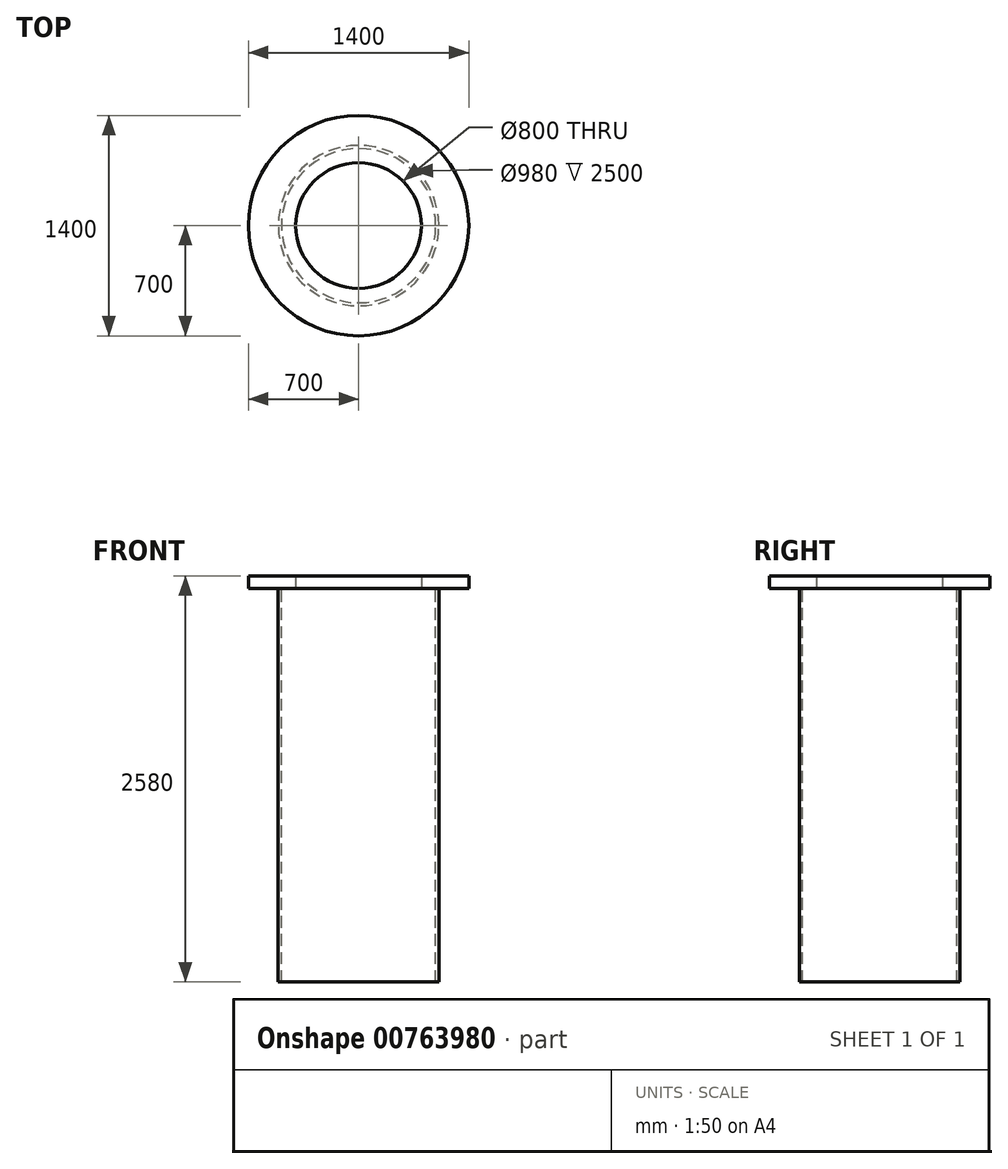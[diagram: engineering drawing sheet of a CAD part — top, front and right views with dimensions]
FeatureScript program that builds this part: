
annotation { "Feature Type Name" : "Feature", "Feature Type Description" : "" }
export const myFeature = defineFeature(function(context is Context, id is Id, definition is map)
    precondition{}
    {
        {
            var Q0;
            Q0=qCreatedBy(makeId("Top.planeOp"),FACE);
            var sketch = newSketch(context, id + "F0", { "sketchPlane" : qUnion([Q0])});
            skCircle(sketch, "E0", {"center": v(0, 0) * mm, "radius": 500 * mm, "construction": true});
            skCircle(sketch, "E1", {"center": v(0, 0) * mm, "radius": 490 * mm});
            skCircle(sketch, "E2", {"center": v(0, 0) * mm, "radius": 510 * mm});
            skCircle(sketch, "E3", {"center": v(0, 0) * mm, "radius": 400 * mm});
            skCircle(sketch, "E4", {"center": v(0, 0) * mm, "radius": 700 * mm});
            skSolve(sketch);
        }
        {
            var Q0;
            Q0=makeQuery(id+"F0.imprint","IMPRINT",FACE,{"disambiguationData":[TD([[makeQuery(id+"F0.imprint","IMPRINT",EDGE,{"derivedFrom":sQuery(id+"F0.wireOp",EDGE,"E1")}),-1.0]])]});
            extrude(context, id + "F1", {"entities" : qUnion([Q0]), "oppositeDirection" : true, "depth" : 2500 * mm, "offsetDistance" : 25 * mm});
        }
        {
            var Q0;
            Q0=makeQuery(id+"F0.imprint","IMPRINT",FACE,{"disambiguationData":[TD([[makeQuery(id+"F0.imprint","IMPRINT",EDGE,{"derivedFrom":sQuery(id+"F0.wireOp",EDGE,"E1")}),1.0]])]});
            var Q1;
            Q1=makeQuery(id+"F0.imprint","IMPRINT",FACE,{"disambiguationData":[TD([[makeQuery(id+"F0.imprint","IMPRINT",EDGE,{"derivedFrom":sQuery(id+"F0.wireOp",EDGE,"E1")}),-1.0]])]});
            var Q2;
            Q2=makeQuery(id+"F0.imprint","IMPRINT",FACE,{"disambiguationData":[TD([[makeQuery(id+"F0.imprint","IMPRINT",EDGE,{"derivedFrom":sQuery(id+"F0.wireOp",EDGE,"E2")}),-1.0]])]});
            extrude(context, id + "F2", {"entities" : qUnion([Q0, Q1, Q2]), "depth" : 80 * mm, "offsetDistance" : 25 * mm});
        }
    });
